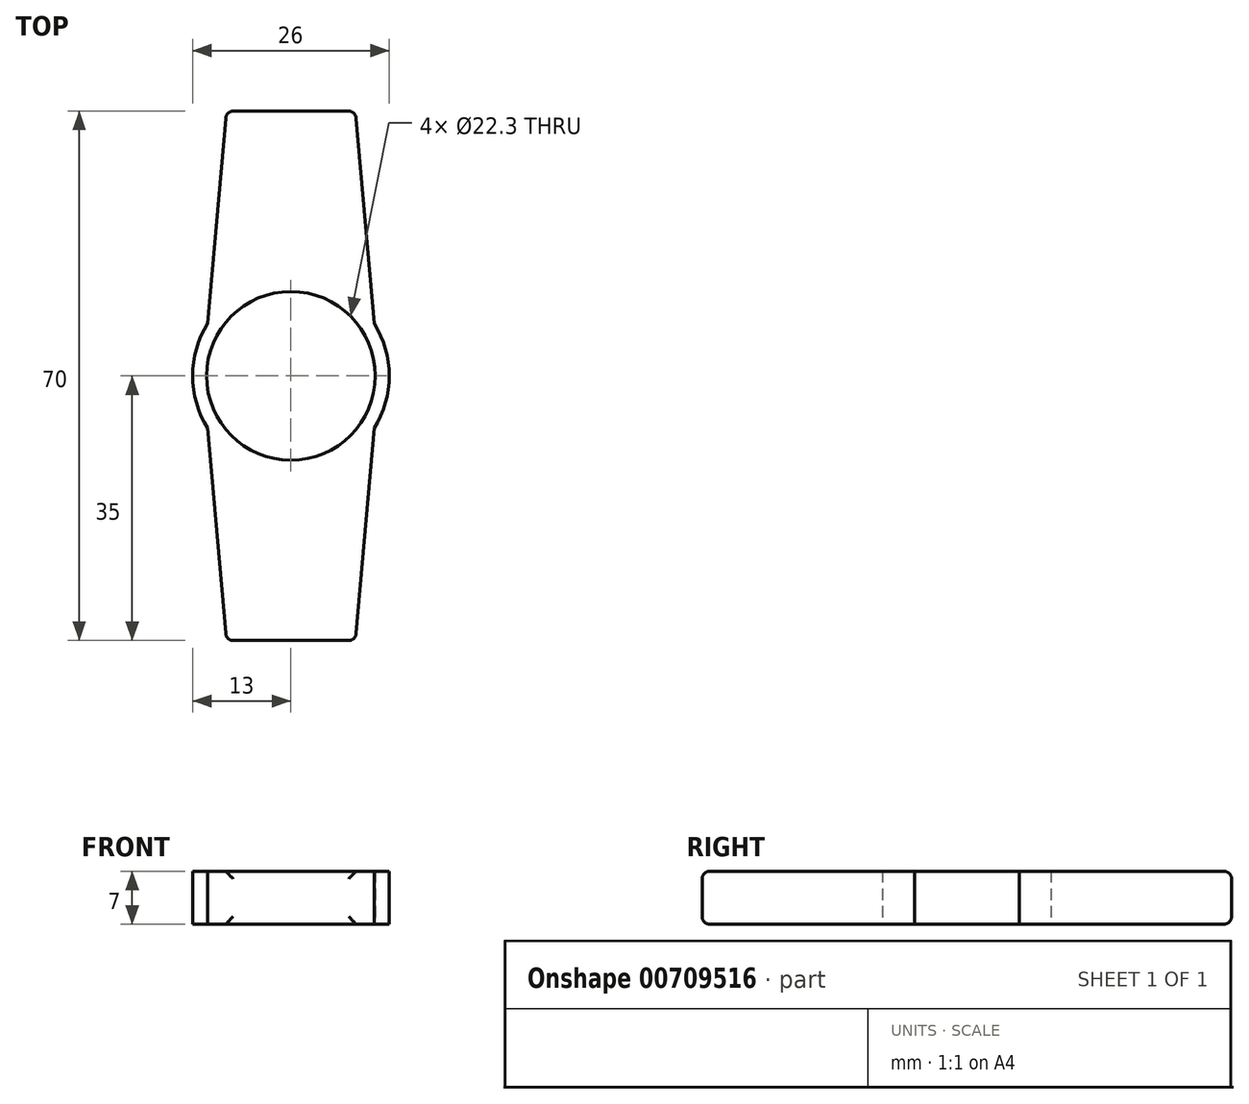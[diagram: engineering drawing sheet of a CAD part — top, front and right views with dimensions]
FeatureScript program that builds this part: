
annotation { "Feature Type Name" : "Feature", "Feature Type Description" : "" }
export const myFeature = defineFeature(function(context is Context, id is Id, definition is map)
    precondition{}
    {
        {
            var Q0;
            Q0=qCreatedBy(makeId("Top.planeOp"),FACE);
            var sketch = newSketch(context, id + "F0", { "sketchPlane" : qUnion([Q0])});
            skCircle(sketch, "E0", {"center": v(0, 0) * mm, "radius": 11.15 * mm});
            skCircle(sketch, "E1", {"center": v(0, 0) * mm, "radius": 13 * mm});
            skLineSegment(sketch, "E2", {"start": v(-11, 6.93) * mm, "end": v(-8.54, 35) * mm});
            skLineSegment(sketch, "E3", {"start": v(-8.54, 35) * mm, "end": v(0, 35) * mm});
            skLineSegment(sketch, "E4.MirrorCS", {"start": v(11, 6.93) * mm, "end": v(8.54, 35) * mm});
            skLineSegment(sketch, "E5.MirrorCS", {"start": v(8.54, 35) * mm, "end": v(0, 35) * mm});
            skLineSegment(sketch, "E6.MirrorCS", {"start": v(8.54, -35) * mm, "end": v(0, -35) * mm});
            skLineSegment(sketch, "E7.MirrorCS", {"start": v(11, -6.93) * mm, "end": v(8.54, -35) * mm});
            skLineSegment(sketch, "E8.MirrorCS", {"start": v(-11, -6.93) * mm, "end": v(-8.54, -35) * mm});
            skLineSegment(sketch, "E9.MirrorCS", {"start": v(-8.54, -35) * mm, "end": v(0, -35) * mm});
            skSolve(sketch);
        }
        {
            var Q0;
            Q0=makeQuery(id+"F0.imprint","IMPRINT",FACE,{"disambiguationData":[TD([[makeQuery(id+"F0.imprint","IMPRINT",EDGE,{"derivedFrom":sQuery(id+"F0.wireOp",EDGE,"E0")}),-1.0]])]});
            var Q1;
            {var subQ1=sQuery(id+"F0.wireOp",EDGE,"E2");Q1=makeQuery(id+"F0.imprint","IMPRINT",FACE,{"disambiguationData":[TD([[makeQuery(id+"F0.imprint","IMPRINT",EDGE,{"derivedFrom":subQ1}),-1.0]])]});}
            var Q2;
            Q2=makeQuery(id+"F0.imprint","IMPRINT",FACE,{"disambiguationData":[TD([[makeQuery(id+"F0.imprint","IMPRINT",EDGE,{"derivedFrom":sQuery(id+"F0.wireOp",EDGE,"E6.MirrorCS")}),-1.0]])]});
            extrude(context, id + "F1", {"entities" : qUnion([Q0, Q1, Q2]), "depth" : 7 * mm, "offsetDistance" : 25 * mm});
        }
        {
            var Q0;
            Q0=makeQuery(id+"F1.opExtrude","SWEPT_FACE",FACE,{"disambiguationData":[OSD([sQuery(id+"F0.wireOp",EDGE,"E6.MirrorCS"),sQuery(id+"F0.wireOp",EDGE,"E9.MirrorCS")])]});
            var Q1;
            Q1=makeQuery(id+"F1.opExtrude","SWEPT_FACE",FACE,{"disambiguationData":[OSD([sQuery(id+"F0.wireOp",EDGE,"E3"),sQuery(id+"F0.wireOp",EDGE,"E5.MirrorCS")])]});
            var Q2;
            {var subQ0=sQuery(id+"F0.wireOp",EDGE,"E1");Q2=makeQuery(id+"F1.opExtrude","SWEPT_FACE",FACE,{"disambiguationData":[OSD([subQ0]),TDD([makeQuery(id+"F0.imprint","IMPRINT",EDGE,{"disambiguationData":[TD([[makeQuery(id+"F0.imprint","INTERSECT",VERTEX,{"derivedFrom":[subQ0,sQuery(id+"F0.wireOp",EDGE,"E4.MirrorCS")]}),-1.0]])],"derivedFrom":subQ0})])]});}
            var Q3;
            {var subQ0=sQuery(id+"F0.wireOp",EDGE,"E1");Q3=makeQuery(id+"F1.opExtrude","SWEPT_FACE",FACE,{"disambiguationData":[OSD([subQ0]),TDD([makeQuery(id+"F0.imprint","IMPRINT",EDGE,{"disambiguationData":[TD([[makeQuery(id+"F0.imprint","INTERSECT",VERTEX,{"derivedFrom":[sQuery(id+"F0.wireOp",EDGE,"E2"),subQ0]}),1.0]])],"derivedFrom":subQ0})])]});}
            fillet(context, id + "F2", {"entities" : qUnion([Q0, Q1, Q2, Q3]), "radius" : 1 * mm, "tangentPropagation" : true, "allowEdgeOverflow" : false});
        }
    });
